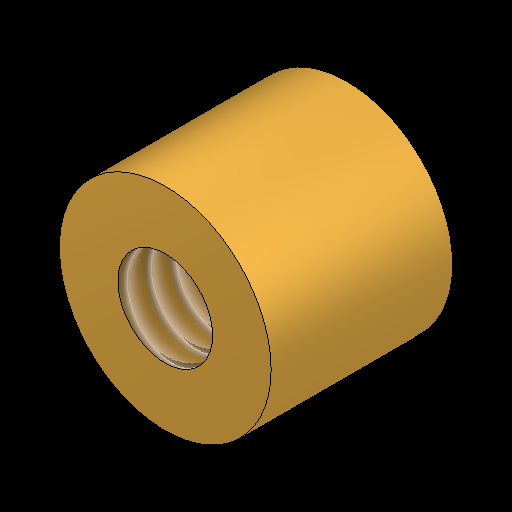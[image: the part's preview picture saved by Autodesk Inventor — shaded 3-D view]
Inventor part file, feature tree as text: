
AUTODESK INVENTOR PART (.ipt)
format: ipt  version: 2023.2 (Build 272271030, 271C)  size: 125,952 bytes
history: native  units: mm
features: sketch x2, extrude x1, hole x1
ambient origin geometry x8: Origin, YZ Plane, XZ Plane, XY Plane, X Axis, Y Axis, Z Axis, Center Point
bodies: Solid1 (feature_tree)
feature tree (4):
  extrude  "Extrusion1"  Depth=3.0mm TaperAngle=0.0deg
  hole  "Hole1"  [1 undecoded]
  sketch  "Sketch1"  dims[d0=3.5mm d1=3.0mm d2=0.0mm]
  sketch  "Sketch2"  dims[d3=1.567mm d4=4.0mm d5=4.0mm d6=2.0mm d7=90.0deg d8=6.3mm d9=20.594885mm]
note: 1 required parameter value undecoded (feature->parameter linkage not recoverable at this tier; creation-order binding heuristic only, values carry confidence <= 0.55)
